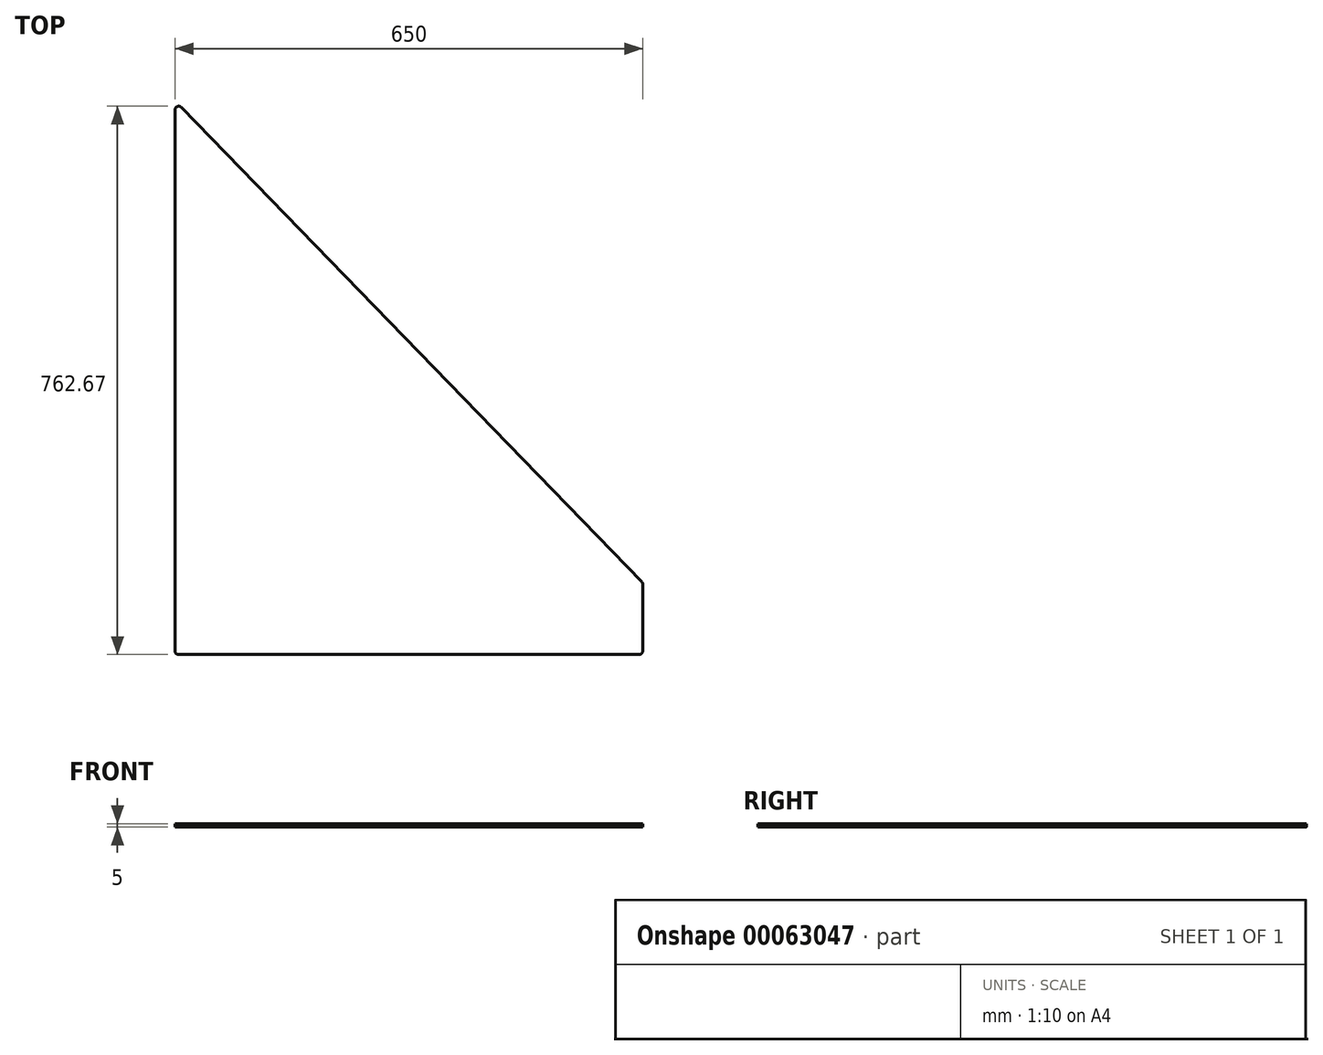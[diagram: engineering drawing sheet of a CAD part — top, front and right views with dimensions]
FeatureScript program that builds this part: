
annotation { "Feature Type Name" : "Feature", "Feature Type Description" : "" }
export const myFeature = defineFeature(function(context is Context, id is Id, definition is map)
    precondition{}
    {
        {
            var Q0;
            Q0=qCreatedBy(makeId("Top.planeOp"),FACE);
            var sketch = newSketch(context, id + "F0", { "sketchPlane" : qUnion([Q0])});
            skLineSegment(sketch, "E0", {"start": v(-5, 0) * mm, "end": v(-645, 0) * mm});
            skLineSegment(sketch, "E1", {"start": v(-650, 5) * mm, "end": v(-650, 757.67) * mm});
            skLineSegment(sketch, "E2", {"start": v(-641.41, 761.15) * mm, "end": v(-1.41, 101.45) * mm});
            skLineSegment(sketch, "E3", {"start": v(0, 97.97) * mm, "end": v(0, 5) * mm});
            skPoint(sketch, "E4.visualSharp", {"position": v(-650, 0) * mm});
            skArc(sketch, "E4.filletArc", {"start": v(-650, 5) * mm, "mid": v(-648.54, 1.46) * mm, "end": v(-645, 0) * mm});
            skPoint(sketch, "E5.visualSharp", {"position": v(0, 0) * mm});
            skArc(sketch, "E5.filletArc", {"start": v(-5, 0) * mm, "mid": v(-1.46, 1.46) * mm, "end": v(0, 5) * mm});
            skPoint(sketch, "E6.visualSharp", {"position": v(-650, 770) * mm});
            skArc(sketch, "E6.filletArc", {"start": v(-641.41, 761.15) * mm, "mid": v(-646.88, 762.3) * mm, "end": v(-650, 757.67) * mm});
            skPoint(sketch, "E7.visualSharp", {"position": v(0, 100) * mm});
            skArc(sketch, "E7.filletArc", {"start": v(0, 97.97) * mm, "mid": v(-0.37, 99.85) * mm, "end": v(-1.41, 101.45) * mm});
            skSolve(sketch);
        }
        {
            var Q0;
            Q0=makeQuery(id+"F0.imprint","IMPRINT",FACE,{"disambiguationData":[TD([[makeQuery(id+"F0.imprint","IMPRINT",EDGE,{"derivedFrom":sQuery(id+"F0.wireOp",EDGE,"E0")}),-1.0]])]});
            extrude(context, id + "F1", {"entities" : qUnion([Q0]), "depth" : 5 * mm});
        }
    });
